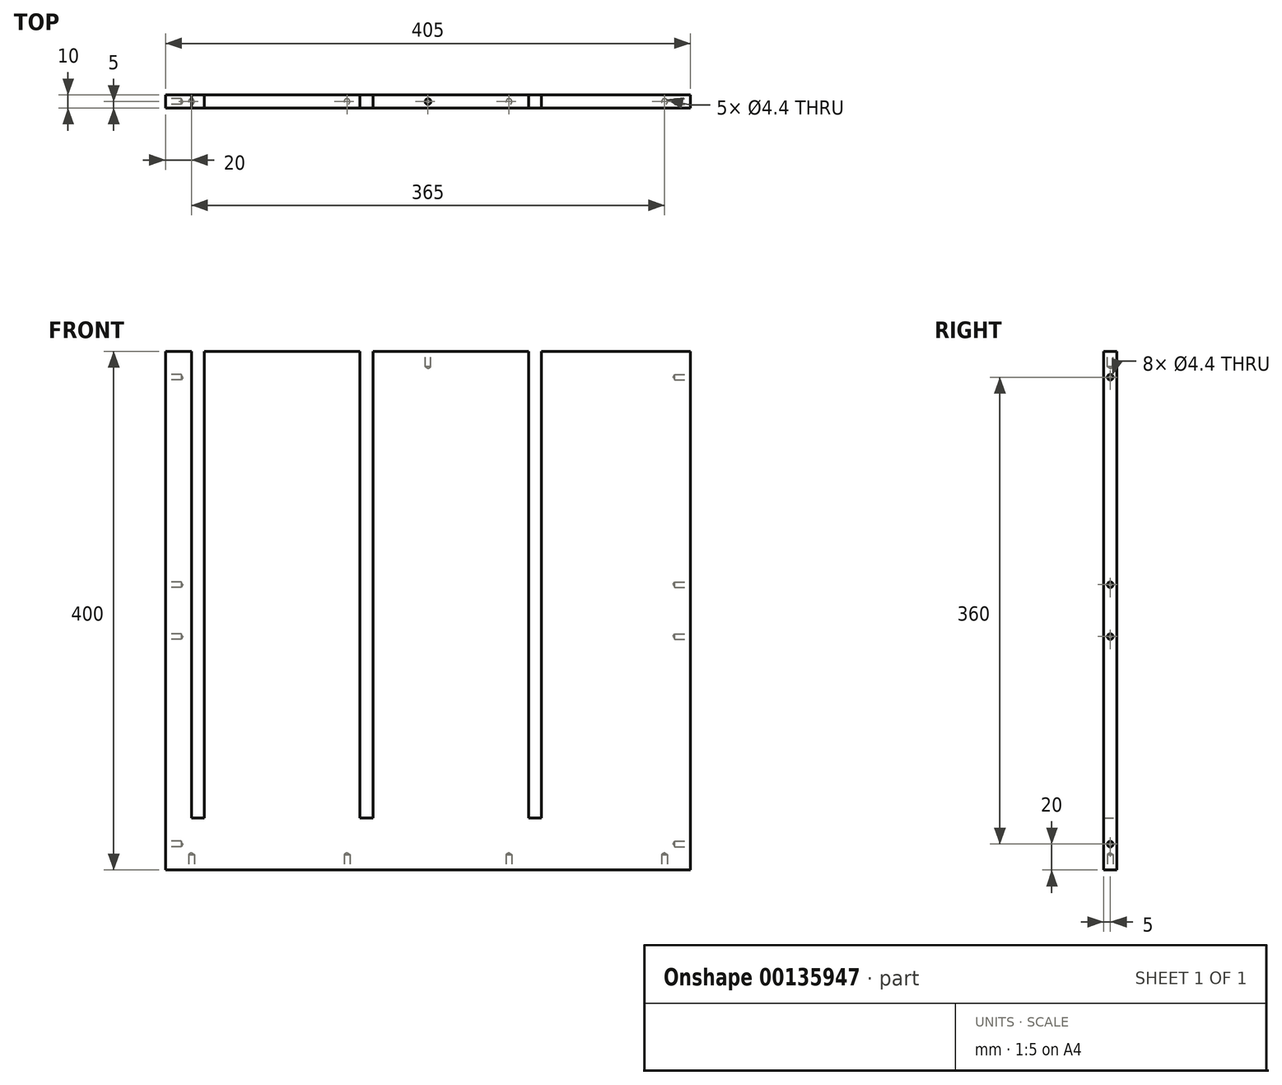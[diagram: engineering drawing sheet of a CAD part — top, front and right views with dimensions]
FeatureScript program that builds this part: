
annotation { "Feature Type Name" : "Feature", "Feature Type Description" : "" }
export const myFeature = defineFeature(function(context is Context, id is Id, definition is map)
    precondition{}
    {
        {
            var Q0;
            Q0=qCreatedBy(makeId("Front.planeOp"),FACE);
            var sketch = newSketch(context, id + "F0", { "sketchPlane" : qUnion([Q0])});
            skLineSegment(sketch, "E0.bottom", {"start": v(202.5, -200) * mm, "end": v(-202.5, -200) * mm});
            skLineSegment(sketch, "E0.top", {"start": v(202.5, 200) * mm, "end": v(-202.5, 200) * mm});
            skLineSegment(sketch, "E0.left", {"start": v(202.5, -200) * mm, "end": v(202.5, 200) * mm});
            skLineSegment(sketch, "E0.right", {"start": v(-202.5, -200) * mm, "end": v(-202.5, 200) * mm});
            skPoint(sketch, "E0.middle", {"position": v(0, 0) * mm});
            skLineSegment(sketch, "E1.bottom", {"start": v(-182.5, 200) * mm, "end": v(-172.5, 200) * mm});
            skLineSegment(sketch, "E1.top", {"start": v(-182.5, -160) * mm, "end": v(-172.5, -160) * mm});
            skLineSegment(sketch, "E1.left", {"start": v(-182.5, 200) * mm, "end": v(-182.5, -160) * mm});
            skLineSegment(sketch, "E1.right", {"start": v(-172.5, 200) * mm, "end": v(-172.5, -160) * mm});
            skLineSegment(sketch, "E2.1.0.0", {"start": v(-52.5, 200) * mm, "end": v(-42.5, 200) * mm});
            skLineSegment(sketch, "E2.1.0.1", {"start": v(-52.5, 200) * mm, "end": v(-52.5, -160) * mm});
            skLineSegment(sketch, "E2.1.0.2", {"start": v(-42.5, 200) * mm, "end": v(-42.5, -160) * mm});
            skLineSegment(sketch, "E2.1.0.3", {"start": v(-52.5, -160) * mm, "end": v(-42.5, -160) * mm});
            skLineSegment(sketch, "E2.2.0.0", {"start": v(77.5, 200) * mm, "end": v(87.5, 200) * mm});
            skLineSegment(sketch, "E2.2.0.1", {"start": v(77.5, 200) * mm, "end": v(77.5, -160) * mm});
            skLineSegment(sketch, "E2.2.0.2", {"start": v(87.5, 200) * mm, "end": v(87.5, -160) * mm});
            skLineSegment(sketch, "E2.2.0.3", {"start": v(77.5, -160) * mm, "end": v(87.5, -160) * mm});
            skLineSegment(sketch, "E2.direction1", {"start": v(-182.5, 200) * mm, "end": v(-52.5, 200) * mm, "construction": true});
            skSolve(sketch);
        }
        {
            var Q0;
            Q0=makeQuery(id+"F0.imprint","IMPRINT",FACE,{"disambiguationData":[TD([[makeQuery(id+"F0.imprint","IMPRINT",EDGE,{"derivedFrom":sQuery(id+"F0.wireOp",EDGE,"E0.bottom")}),-1.0]])]});
            extrude(context, id + "F1", {"entities" : qUnion([Q0]), "endBound" : BoundingType.SYMMETRIC, "depth" : 10 * mm});
        }
        {
            var Q0;
            Q0=makeQuery(id+"F1.opExtrude","SWEPT_FACE",FACE,{"disambiguationData":[OSD([sQuery(id+"F0.wireOp",EDGE,"E0.top")])]});
            var sketch = newSketch(context, id + "F2", { "sketchPlane" : qUnion([Q0])});
            skCircle(sketch, "E3", {"center": v(0, 0) * mm, "radius": 2 * mm});
            skSolve(sketch);
        }
        {
            var Q0;
            Q0=makeQuery(id+"F1.opExtrude","SWEPT_FACE",FACE,{"disambiguationData":[OSD([sQuery(id+"F0.wireOp",EDGE,"E0.right")])]});
            var sketch = newSketch(context, id + "F3", { "sketchPlane" : qUnion([Q0])});
            skCircle(sketch, "E4", {"center": v(0, -180) * mm, "radius": 2 * mm});
            skCircle(sketch, "E5", {"center": v(0, -20) * mm, "radius": 2 * mm});
            skCircle(sketch, "E6.MirrorC", {"center": v(0, 20) * mm, "radius": 2 * mm});
            skCircle(sketch, "E7.MirrorC", {"center": v(0, 180) * mm, "radius": 2 * mm});
            skSolve(sketch);
        }
        {
            var Q0;
            Q0=makeQuery(id+"F1.opExtrude","SWEPT_FACE",FACE,{"disambiguationData":[OSD([sQuery(id+"F0.wireOp",EDGE,"E0.left")])]});
            var sketch = newSketch(context, id + "F4", { "sketchPlane" : qUnion([Q0])});
            skCircle(sketch, "E8", {"center": v(0, -180) * mm, "radius": 2 * mm});
            skCircle(sketch, "E9", {"center": v(0, -20) * mm, "radius": 2 * mm});
            skCircle(sketch, "E10.MirrorC", {"center": v(0, 180) * mm, "radius": 2 * mm});
            skCircle(sketch, "E11.MirrorC", {"center": v(0, 20) * mm, "radius": 2 * mm});
            skSolve(sketch);
        }
        {
            var Q0;
            Q0=makeQuery(id+"F1.opExtrude","SWEPT_FACE",FACE,{"disambiguationData":[OSD([sQuery(id+"F0.wireOp",EDGE,"E0.bottom")])]});
            var sketch = newSketch(context, id + "F5", { "sketchPlane" : qUnion([Q0])});
            skCircle(sketch, "E12", {"center": v(-182.5, 0) * mm, "radius": 2 * mm});
            skCircle(sketch, "E13", {"center": v(-62.5, 0) * mm, "radius": 2 * mm});
            skCircle(sketch, "E14.MirrorC", {"center": v(62.5, 0) * mm, "radius": 2 * mm});
            skCircle(sketch, "E15.MirrorC", {"center": v(182.5, 0) * mm, "radius": 2 * mm});
            skSolve(sketch);
        }
        {
            var Q0;
            Q0=sQuery(id+"F2.wireOp",VERTEX,"6Lffy2n0-Hwvo-p07d-KwoW-lIIL1oFBVM86.center");
            var Q1;
            Q1=sQuery(id+"F2.wireOp",VERTEX,"E3.center");
            var Q2;
            Q2=sQuery(id+"F2.wireOp",VERTEX,"N0LrrZqT-inZq-m3Pn-OrCf-dQQlCZNRCZq6.center");
            var Q3;
            Q3=makeQuery(id+"F1.opExtrude","SWEPT_BODY",BODY,{"disambiguationData":[OSD([sQuery(id+"F0.wireOp",EDGE,"E0.bottom"),sQuery(id+"F0.wireOp",EDGE,"E0.top"),sQuery(id+"F0.wireOp",EDGE,"E0.left"),sQuery(id+"F0.wireOp",EDGE,"E0.right"),sQuery(id+"F0.wireOp",EDGE,"XWZrsFJl-hZ8c-8RFI-7IJq-EzOZ3sIGLfD4"),sQuery(id+"F0.wireOp",EDGE,"QB0C6CPn-qOL8-fIRA-QjEU-Y9BwwvSa6pRB"),sQuery(id+"F0.wireOp",EDGE,"G4GAvN2Z-Aj42-7Is6-4Fkr-iGkbHWXBV4Qq"),sQuery(id+"F0.wireOp",EDGE,"ztsScnvx-69nE-OQe9-Xu7z-F3aSEwL5bO77"),sQuery(id+"F0.wireOp",EDGE,"QAZC7S4a-mdPt-mVvo-yF0x-VzN3XJBQlE6b"),sQuery(id+"F0.wireOp",EDGE,"MX8Ww9h4-DqsU-lgLO-alZj-Cp6TfRqocJF7")])]});
            hole(context, id + "F6", {"style" : HoleStyle.SIMPLE, "endStyle" : HoleEndStyle.BLIND, "standardTappedOrClearance" : lookupTablePath({ "standard" : "ISO", "fit" : "Normal", "size" : "M4", "type" : "Clearance" }), "standardBlindInLast" : lookupTablePath({ "fit" : "Standard", "standard" : "ISO", "size" : "M4", "type" : "Clearance" }), "holeDiameter" : 4.4 * mm, "holeDepth" : 12 * mm, "locations" : qUnion([Q0, Q1, Q2]), "scope" : qUnion([Q3])});
        }
        {
            var Q0;
            Q0=sQuery(id+"F3.wireOp",VERTEX,"E4.center");
            var Q1;
            Q1=sQuery(id+"F3.wireOp",VERTEX,"qqGtBSmb-rbsb-Fcsp-kRQr-C2yqoKzzYkRx.center");
            var Q2;
            Q2=sQuery(id+"F3.wireOp",VERTEX,"np5yDtHH-8xK2-o30u-uAzj-AooPbOI2qIzy.center");
            var Q3;
            Q3=sQuery(id+"F4.wireOp",VERTEX,"96BtO6sM-U9Rg-BRqU-L3c4-5XYo4Ebyo1ly.center");
            var Q4;
            Q4=sQuery(id+"F4.wireOp",VERTEX,"eGXLnyBz-7oUu-Rtn7-jFfd-iT3XmmhfMEnJ.center");
            var Q5;
            Q5=sQuery(id+"F4.wireOp",VERTEX,"E8.center");
            var Q6;
            Q6=sQuery(id+"F4.wireOp",VERTEX,"E9.center");
            var Q7;
            Q7=sQuery(id+"F4.wireOp",VERTEX,"Qm1q9ucX-QW7I-lIMD-vBtR-auPxus0JihbM.center");
            var Q8;
            Q8=sQuery(id+"F3.wireOp",VERTEX,"5M1S5MDJ-yu4y-kJTk-Zwr1-ycYVcb5nf2MM.center");
            var Q9;
            Q9=sQuery(id+"F3.wireOp",VERTEX,"E5.center");
            var Q10;
            Q10=sQuery(id+"F4.wireOp",VERTEX,"E10.MirrorC.center");
            var Q11;
            Q11=sQuery(id+"F4.wireOp",VERTEX,"E11.MirrorC.center");
            var Q12;
            Q12=sQuery(id+"F3.wireOp",VERTEX,"E6.MirrorC.center");
            var Q13;
            Q13=sQuery(id+"F3.wireOp",VERTEX,"E7.MirrorC.center");
            var Q14;
            Q14=sQuery(id+"F5.wireOp",VERTEX,"E12.center");
            var Q15;
            Q15=sQuery(id+"F5.wireOp",VERTEX,"E13.center");
            var Q16;
            Q16=sQuery(id+"F5.wireOp",VERTEX,"E14.MirrorC.center");
            var Q17;
            Q17=sQuery(id+"F5.wireOp",VERTEX,"E15.MirrorC.center");
            var Q18;
            Q18=makeQuery(id+"F1.opExtrude","SWEPT_BODY",BODY,{"disambiguationData":[OSD([sQuery(id+"F0.wireOp",EDGE,"E0.bottom"),sQuery(id+"F0.wireOp",EDGE,"E0.top"),sQuery(id+"F0.wireOp",EDGE,"E0.left"),sQuery(id+"F0.wireOp",EDGE,"E0.right")])]});
            hole(context, id + "F7", {"style" : HoleStyle.SIMPLE, "endStyle" : HoleEndStyle.BLIND, "standardTappedOrClearance" : lookupTablePath({ "standard" : "ISO", "fit" : "Normal", "size" : "M4", "type" : "Clearance" }), "standardBlindInLast" : lookupTablePath({ "fit" : "Standard", "standard" : "ISO", "size" : "M4", "type" : "Clearance" }), "holeDiameter" : 4.4 * mm, "holeDepth" : 12 * mm, "startFromSketch" : true, "locations" : qUnion([Q0, Q1, Q2, Q3, Q4, Q5, Q6, Q7, Q8, Q9, Q10, Q11, Q12, Q13, Q14, Q15, Q16, Q17]), "scope" : qUnion([Q18])});
        }
    });
